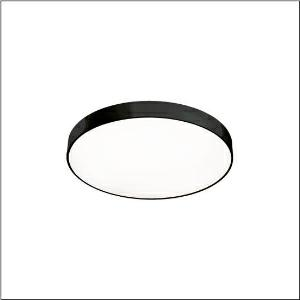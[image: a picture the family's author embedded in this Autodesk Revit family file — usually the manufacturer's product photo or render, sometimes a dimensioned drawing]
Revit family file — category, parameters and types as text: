
# Revit family: round_21_m_51mr36fd0321b
name_source: partatom
category: Lighting Fixtures
units: mm (PartAtom-declared; Revit-internal decimal feet)

## family parameters
Cut with Voids When Loaded = No
Host = Face
Light Source = No
Part Type = Normal
Room Calculation Point = No
Round Connector Dimension = Use Diameter
Shared = No

## types (1)
- Round 21 M (1 x LED, 6790 lm, 54.8 W, 3000K)
    Apparent Load = 55 VA
    CIE Flux Codes = 49 80 96 100 100
    Color Rendering = 80
    Color Temperature = 3000K
    Default Elevation = 1800 mm
    Description = Round 21 M, wall and ceiling luminaire, primary optical cover: cover, of PMMA, opal, light emission: direct distribution, primary light characteristic: symmetric, installation type: suspended mounting, surface-mounted, LED, rated luminous flux: 6.790lm, luminous efficacy: 124lm/W, light colour: 830, colour temperature: 3000K, with terminal, 5-pole, mains connection: 230V, AC, 50/60Hz, rated input power: 55W, housing, of aluminium, coated, black, diameter: 600mm, height: 62mm, protection rating (complete): IP40, insulation class (complete): insulation class I (protective earthing), certification: CE, impact resistance: IK04, permissible operating ambient temperature: -10..+35°C, packaging unit: 1 piece
    Height = 87 mm
    Lamp = 1 x LED
    Lamp Light Flux = 6790 lm
    Lamp Power = 54.8 W
    Lamp count = 1
    Length = 600 mm
    Luminous efficacy = 124 lm/W
    Manufacturer = Siteco
    ModVariant = No
    Model = 51MR36FD0321B
    Mounting Place = Ceiling
    Mounting Type = Surface mounted
    Number of Poles = 1
    OnlyDefault = Yes
    Power Factor = 1
    Product Name = Round 21 M
    Product group = wall and ceiling luminaire
    ProductGroupID = 302
    Protection Class = Protection class I
    Protection Degree = IP 40
    RLX_Detail_Level = 1
    RLX_Emergency_Light_Flux = 0 lm
    RLX_Emergency_Type = 0
    RLX_Emergency_Type_DB = No
    RlxData = <blob elided: 17701 chars, md5=29e610a3>
    Socket = socket
    Standby Power = 0 W
    System Light Flux = 6790 lm
    System Power = 55 W
    Type Comments = Product without accessories
    Type Image = l_1258332.jpg
    URL = http://relux.com
    VarID = ---
    Voltage = 0 V
    Weight = 0.00 kg
    Width = 0 mm  [stored 0 ft]

note: [stored X ft] marks values corroborated as IEEE doubles in the binary element streams (Revit-internal decimal feet)

## geometry (parser evidence)
native form markers: Blend x4, Sweep x10
no freeform markers — native parametric forms only
